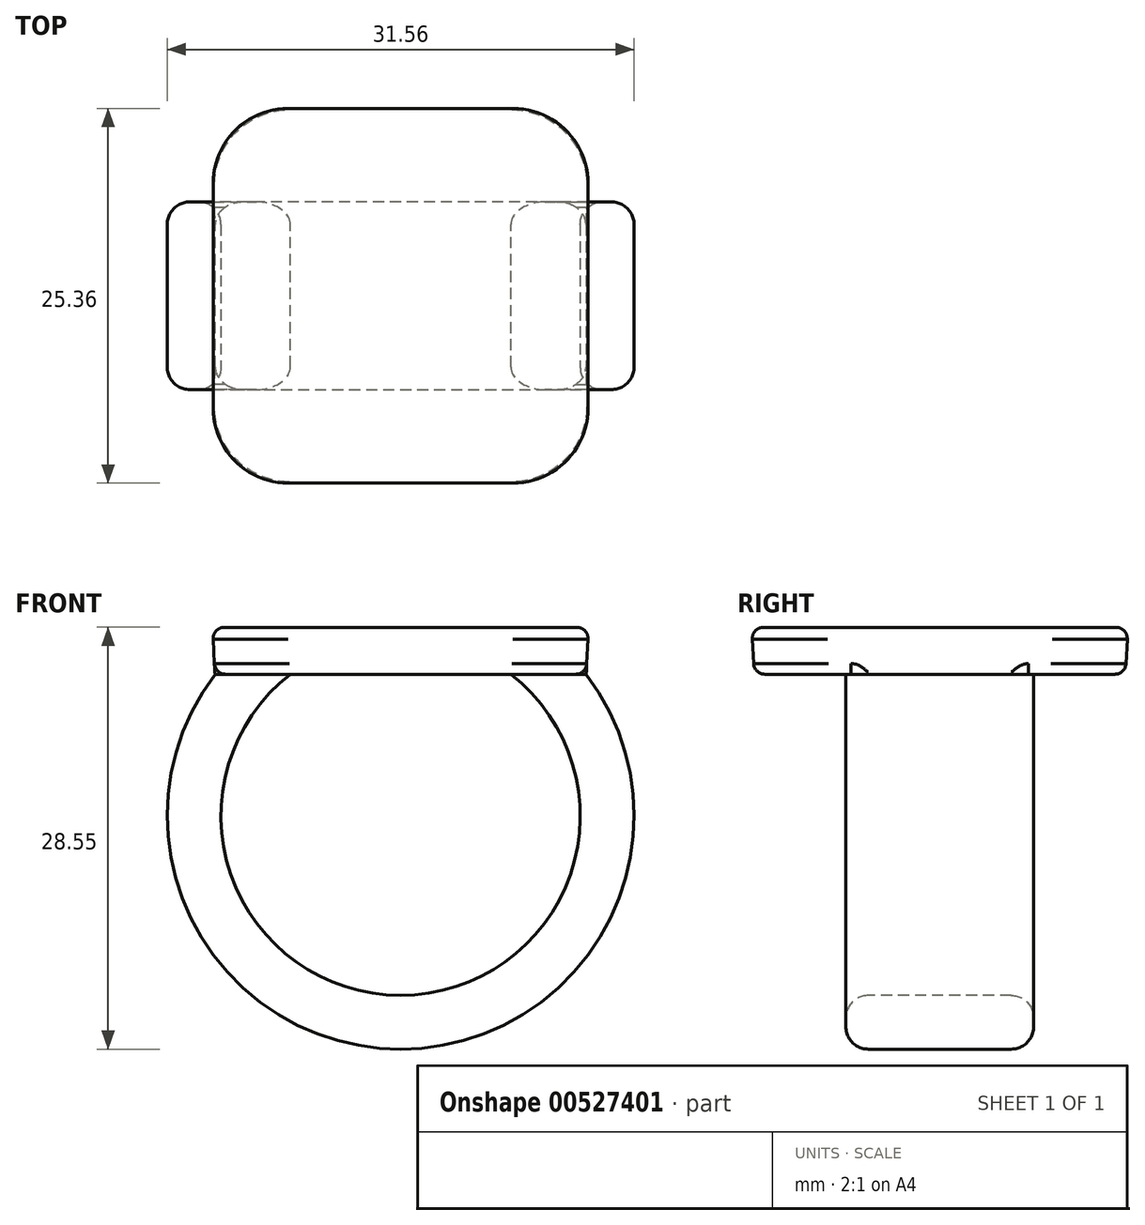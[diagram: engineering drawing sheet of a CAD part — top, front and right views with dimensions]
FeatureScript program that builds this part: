
annotation { "Feature Type Name" : "Feature", "Feature Type Description" : "" }
export const myFeature = defineFeature(function(context is Context, id is Id, definition is map)
    precondition{}
    {
        {
            var Q0;
            Q0=qCreatedBy(makeId("Top.planeOp"),FACE);
            var sketch = newSketch(context, id + "F0", { "sketchPlane" : qUnion([Q0])});
            skLineSegment(sketch, "E0.bottom", {"start": v(-12.55, 12.55) * mm, "end": v(12.55, 12.55) * mm});
            skLineSegment(sketch, "E0.top", {"start": v(-12.55, -12.55) * mm, "end": v(12.55, -12.55) * mm});
            skLineSegment(sketch, "E0.left", {"start": v(-12.55, 12.55) * mm, "end": v(-12.55, -12.55) * mm});
            skLineSegment(sketch, "E0.right", {"start": v(12.55, 12.55) * mm, "end": v(12.55, -12.55) * mm});
            skPoint(sketch, "E0.middle", {"position": v(0, 0) * mm});
            skSolve(sketch);
        }
        {
            var Q0;
            Q0 = qSketchRegion(id + "F0", true);
            extrude(context, id + "F1", {"entities" : qUnion([Q0]), "depth" : 3.17 * mm, "offsetDistance" : 25.4 * mm, "hasDraft" : true, "draftAngle" : 3 * degree});
        }
        {
            var Q0;
            Q0=qCreatedBy(makeId("Front.planeOp"),FACE);
            var sketch = newSketch(context, id + "F2", { "sketchPlane" : qUnion([Q0])});
            skArc(sketch, "E1", {"start": v(-10.16, 0) * mm, "mid": v(0, -23.56) * mm, "end": v(10.16, 0) * mm});
            skSolve(sketch);
        }
        {
            var Q0;
            Q0=makeQuery(id+"F1.opExtrude","CAP_FACE",FACE,{"disambiguationData":[OSD([sQuery(id+"F0.wireOp",EDGE,"E0.bottom"),sQuery(id+"F0.wireOp",EDGE,"E0.top"),sQuery(id+"F0.wireOp",EDGE,"E0.left"),sQuery(id+"F0.wireOp",EDGE,"E0.right")])],"isStart":true});
            var sketch = newSketch(context, id + "F3", { "sketchPlane" : qUnion([Q0])});
            skLineSegment(sketch, "E2.bottom", {"start": v(-7.45, 6.35) * mm, "end": v(-12.53, 6.35) * mm});
            skLineSegment(sketch, "E2.top", {"start": v(-7.45, -6.35) * mm, "end": v(-12.53, -6.35) * mm});
            skLineSegment(sketch, "E2.left", {"start": v(-7.45, 6.35) * mm, "end": v(-7.45, -6.35) * mm});
            skLineSegment(sketch, "E2.right", {"start": v(-12.53, 6.35) * mm, "end": v(-12.53, -6.35) * mm});
            skPoint(sketch, "E2.middle", {"position": v(-10, 0) * mm});
            skPoint(sketch, "E2.middle.positionSnap0", {"position": v(-12.55, 0) * mm});
            skPoint(sketch, "E2.centerSnap0", {"position": v(-12.55, 0) * mm});
            skSolve(sketch);
        }
        {
            var Q0;
            Q0 = qSketchRegion(id + "F3", true);
            var Q1;
            Q1 = qConstructionFilter(qBodyType(qCreatedBy(id + "F2" ,EDGE), BodyType.WIRE), ConstructionObject.NO);
            sweep(context, id + "F4", {"operationType" : NewBodyOperationType.ADD, "profiles" : qUnion([Q0]), "path" : qUnion([Q1])});
        }
        {
            var Q0;
            Q0=qCreatedBy(makeId("Front.planeOp"),FACE);
            var sketch = newSketch(context, id + "F5", { "sketchPlane" : qUnion([Q0])});
            skLineSegment(sketch, "E3.1", {"start": v(10, -2.7) * mm, "end": v(10.16, 0) * mm});
            skArc(sketch, "E3.2", {"start": v(10, -2.7) * mm, "mid": v(8.83, -1.25) * mm, "end": v(7.45, 0) * mm});
            skLineSegment(sketch, "E4.trimOffspring", {"start": v(7.45, 0) * mm, "end": v(10.16, 0) * mm});
            skPoint(sketch, "E3.0.start.orphan", {"position": v(-12.55, 0) * mm});
            skPoint(sketch, "E5.orphan", {"position": v(12.55, 0) * mm});
            skPoint(sketch, "E6.orphan", {"position": v(-7.45, 0) * mm});
            skSolve(sketch);
        }
        {
            var Q0;
            Q0 = qSketchRegion(id + "F5", true);
            var Q1;
            Q1=makeQuery(id+"F4.opSweep","SWEPT_FACE",FACE,{"disambiguationData":[OSD([sQuery(id+"F2.wireOp",EDGE,"E1"),sQuery(id+"F3.wireOp",EDGE,"E2.bottom")])]});
            var Q2;
            Q2=makeQuery(id+"F4.opSweep","SWEPT_FACE",FACE,{"disambiguationData":[OSD([sQuery(id+"F2.wireOp",EDGE,"E1"),sQuery(id+"F3.wireOp",EDGE,"E2.top")])]});
            extrude(context, id + "F6", {"entities" : qUnion([Q0]), "operationType" : NewBodyOperationType.ADD, "endBound" : BoundingType.UP_TO_SURFACE, "depth" : 25.4 * mm, "endBoundEntityFace" : qUnion([Q1]), "offsetDistance" : 25.4 * mm, "hasSecondDirection" : true, "secondDirectionBound" : SecondDirectionBoundingType.UP_TO_SURFACE, "secondDirectionOppositeDirection" : true, "secondDirectionDepth" : 25.4 * mm, "secondDirectionBoundEntityFace" : qUnion([Q2])});
        }
        {
            var Q0;
            Q0=makeQuery(id+"F1.opExtrude","SWEPT_EDGE",EDGE,{"disambiguationData":[OSD([sQuery(id+"F0.wireOp",EDGE,"E0.top"),sQuery(id+"F0.wireOp",EDGE,"E0.left")])]});
            var Q1;
            Q1=makeQuery(id+"F1.opExtrude","SWEPT_EDGE",EDGE,{"disambiguationData":[OSD([sQuery(id+"F0.wireOp",EDGE,"E0.bottom"),sQuery(id+"F0.wireOp",EDGE,"E0.right")])]});
            var Q2;
            Q2=makeQuery(id+"F1.opExtrude","SWEPT_EDGE",EDGE,{"disambiguationData":[OSD([sQuery(id+"F0.wireOp",EDGE,"E0.top"),sQuery(id+"F0.wireOp",EDGE,"E0.right")])]});
            var Q3;
            Q3=makeQuery(id+"F1.opExtrude","SWEPT_EDGE",EDGE,{"disambiguationData":[OSD([sQuery(id+"F0.wireOp",EDGE,"E0.bottom"),sQuery(id+"F0.wireOp",EDGE,"E0.left")])]});
            fillet(context, id + "F7", {"entities" : qUnion([Q0, Q1, Q2, Q3]), "radius" : 5.08 * mm, "tangentPropagation" : true, "allowEdgeOverflow" : false});
        }
        {
            var Q0;
            {var subQ0=sQuery(id+"F3.wireOp",EDGE,"E2.bottom");var subQ1=sQuery(id+"F2.wireOp",EDGE,"E1");Q0=makeQuery(id+"F6.boolean.opBoolean","MERGE",EDGE,{"derivedFrom":[makeQuery(id+"F4.opSweep","SWEPT_EDGE",EDGE,{"disambiguationData":[OSD([subQ1,subQ0,sQuery(id+"F3.wireOp",EDGE,"E2.left")])]}),makeQuery(id+"F6.opExtrude","TWEAK_EDGE",EDGE,{"derivedFrom":[makeQuery(id+"F4.opSweep","SWEPT_FACE",FACE,{"disambiguationData":[OSD([subQ1,subQ0])]}),makeQuery(id+"F5.imprint","IMPRINT",EDGE,{"derivedFrom":sQuery(id+"F5.wireOp",EDGE,"E3.2")})]})]});}
            var Q1;
            Q1=makeQuery(id+"F4.opSweep","SWEPT_EDGE",EDGE,{"disambiguationData":[OSD([sQuery(id+"F2.wireOp",EDGE,"E1"),sQuery(id+"F3.wireOp",EDGE,"E2.bottom"),sQuery(id+"F3.wireOp",EDGE,"E2.right")])]});
            var Q2;
            {var subQ0=sQuery(id+"F3.wireOp",EDGE,"E2.top");var subQ1=sQuery(id+"F2.wireOp",EDGE,"E1");Q2=makeQuery(id+"F6.boolean.opBoolean","MERGE",EDGE,{"derivedFrom":[makeQuery(id+"F4.opSweep","SWEPT_EDGE",EDGE,{"disambiguationData":[OSD([subQ1,subQ0,sQuery(id+"F3.wireOp",EDGE,"E2.left")])]}),makeQuery(id+"F6.opExtrude","TWEAK_EDGE",EDGE,{"derivedFrom":[makeQuery(id+"F4.opSweep","SWEPT_FACE",FACE,{"disambiguationData":[OSD([subQ1,subQ0])]}),makeQuery(id+"F5.imprint","IMPRINT",EDGE,{"derivedFrom":sQuery(id+"F5.wireOp",EDGE,"E3.2")})]})]});}
            var Q3;
            Q3=makeQuery(id+"F4.opSweep","SWEPT_EDGE",EDGE,{"disambiguationData":[OSD([sQuery(id+"F2.wireOp",EDGE,"E1"),sQuery(id+"F3.wireOp",EDGE,"E2.top"),sQuery(id+"F3.wireOp",EDGE,"E2.right")])]});
            fillet(context, id + "F8", {"entities" : qUnion([Q0, Q1, Q2, Q3]), "radius" : 1.52 * mm, "tangentPropagation" : true, "allowEdgeOverflow" : false});
        }
        {
            var Q0;
            Q0=makeQuery(id+"F1.opExtrude","CAP_EDGE",EDGE,{"disambiguationData":[OSD([sQuery(id+"F0.wireOp",EDGE,"E0.top")])],"isStart":false});
            var Q1;
            Q1=makeQuery(id+"F1.opExtrude","CAP_EDGE",EDGE,{"disambiguationData":[OSD([sQuery(id+"F0.wireOp",EDGE,"E0.top")])],"isStart":true});
            fillet(context, id + "F9", {"entities" : qUnion([Q0, Q1]), "radius" : 0.76 * mm, "tangentPropagation" : true, "allowEdgeOverflow" : false});
        }
    });
